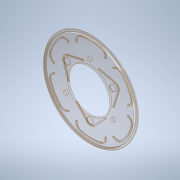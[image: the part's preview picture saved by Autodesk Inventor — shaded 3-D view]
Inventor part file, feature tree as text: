
AUTODESK INVENTOR PART (.ipt)
format: ipt  version: 2020 (Build 240168000, 168)  size: 402,944 bytes
history: native  units: in
note: dims shown in document units (in); Inventor stores cm internally (conversion verified against a paired STEP export)
features: sketch x12, extrude x9, projected_geometry x5, plane x2, shell x1, sweep x1, hole x1
ambient origin geometry x8: Origin, YZ Plane, XZ Plane, XY Plane, X Axis, Y Axis, Z Axis, Center Point
bodies: Solid1 (feature_tree)
feature tree (31):
  extrude  "Extrusion1"  Depth=3.1496in TaperAngle=0.0deg
  shell  "Shell1"  Thickness=0.1181in
  extrude  "Extrusion2"  Depth=3.1496in TaperAngle=0.0deg
  extrude  "Extrusion3"  Depth=1.5748in
  plane  "Work Plane1"
  extrude  "Extrusion4"  TaperAngle=120.0deg  [1 undecoded]
  extrude  "Extrusion5"  Depth=0.378in
  plane  "Work Plane4"
  sweep  "Sweep2"
  extrude  "Extrusion6"  [1 undecoded]
  hole  "Hole1"  [1 undecoded]
  extrude  "Extrusion9"  Depth=0.1181in TaperAngle=0.0deg
  extrude  "Extrusion10"  Depth=0.0591in
  extrude  "Extrusion11"  Depth=0.0591in
  sketch  "Sketch1"  dims[d1=5.3543in d2=3.1496in d3=0.0in d4=0.1181in]
  sketch  "Sketch2"  dims[d5=2.5197in d6=3.1496in d7=0.0in]
  sketch  "Sketch3"  dims[d8=0.378in d9=1.5748in]
  projected_geometry  "Projected Loop1"
  sketch  "Sketch4"  dims[d10=120.0deg d11=120.0deg]
  sketch  "Sketch6"  dims[d12=0.378in d13=0.378in]
  projected_geometry  "Projected Loop3"
  sketch  "Sketch9"  dims[d14=1.5748in d15=1.5748in]
  projected_geometry  "Projected Loop4"
  sketch  "Sketch10"  dims[d16=0.06in d17=0.0in d18=-0.9843in]
  sketch  "Sketch11"  dims[d24=1.1811in d25=0.9843in d26=0.0in]
  projected_geometry  "Projected Loop5"
  sketch  "Sketch14"  dims[d27=0.1181in d28=2.2201in d29=0.0in]
  sketch  "Sketch16"  dims[d37=0.0in d38=0.0in d39=0.0591in]
  sketch  "Sketch17"  dims[d40=0.0591in d41=0.0591in]
  projected_geometry  "Projected Loop7"
  sketch  "Sketch18"  dims[d42=0.0591in d43=0.0591in d44=0.0591in d45=0.0591in d46=0.9843in d47=0.9843in d48=0.9843in d49=0.9843in d50=0.9843in d51=0.9843in d52=0.0591in d53=0.0in d98=0.2362in d99=1.6142in d100=1.1811in d102=360.0deg d104=0.2362in d105=0.2362in d106=0.1575in d107=0.0787in d108=90.0deg d109=0.315in d110=0.8108in d111=0.3937in d112=0.0in d113=0.3937in d114=0.0in d115=5.5906in d116=0.378in d117=5.1181in d118=2.2638in d119=0.0591in d120=0.7874in d121=0.7874in d122=2.3622in d124=360.0deg d126=0.0591in d127=0.0591in d128=2.3622in d130=360.0deg d132=0.0591in d133=0.0in]
note: 3 required parameter values undecoded (feature->parameter linkage not recoverable at this tier; creation-order binding heuristic only, values carry confidence <= 0.55)
